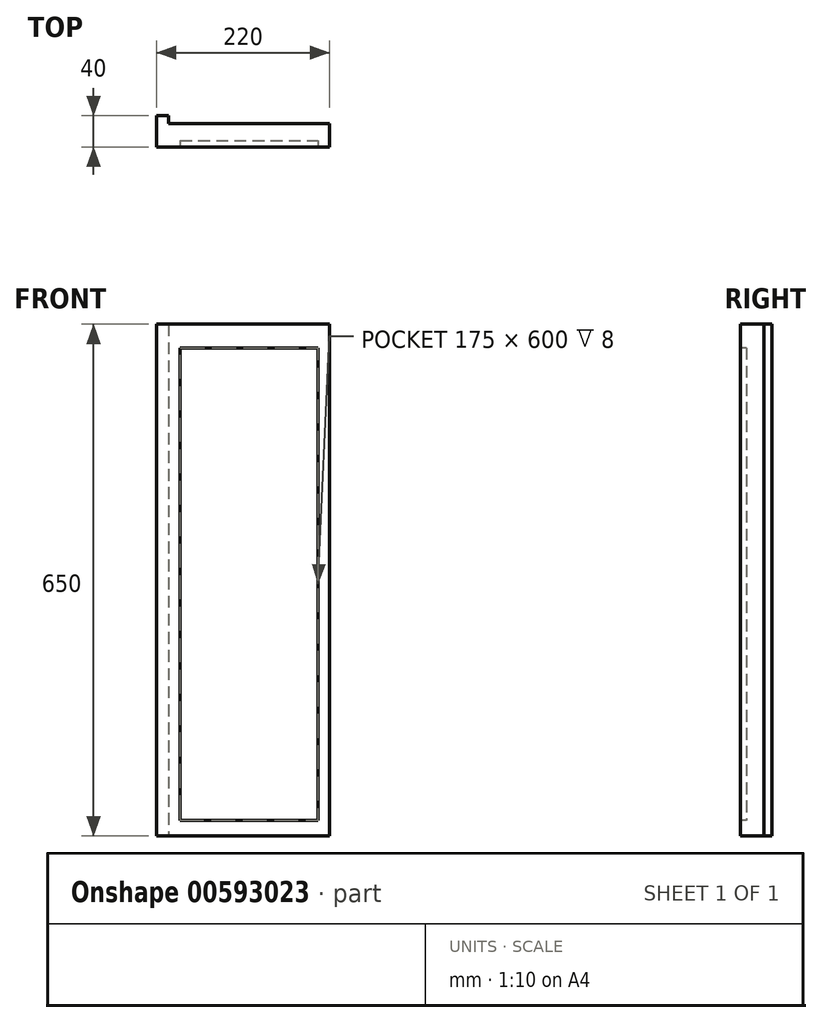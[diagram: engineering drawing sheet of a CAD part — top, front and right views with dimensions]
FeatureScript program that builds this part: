
annotation { "Feature Type Name" : "Feature", "Feature Type Description" : "" }
export const myFeature = defineFeature(function(context is Context, id is Id, definition is map)
    precondition{}
    {
        {
            var Q0;
            Q0=qCreatedBy(makeId("Front.planeOp"),FACE);
            var sketch = newSketch(context, id + "F0", { "sketchPlane" : qUnion([Q0])});
            skLineSegment(sketch, "E0.bottom", {"start": v(0, 0) * mm, "end": v(220, 0) * mm});
            skLineSegment(sketch, "E0.top", {"start": v(0, 650) * mm, "end": v(220, 650) * mm});
            skLineSegment(sketch, "E0.left", {"start": v(0, 0) * mm, "end": v(0, 650) * mm});
            skLineSegment(sketch, "E0.right", {"start": v(220, 0) * mm, "end": v(220, 650) * mm});
            skSolve(sketch);
        }
        {
            var Q0;
            Q0 = qSketchRegion(id + "F0", true);
            extrude(context, id + "F1", {"entities" : qUnion([Q0]), "depth" : 30 * mm, "offsetDistance" : 25 * mm});
        }
        {
            var Q0;
            Q0=makeQuery(id+"F1.opExtrude","CAP_FACE",FACE,{"disambiguationData":[OSD([sQuery(id+"F0.wireOp",EDGE,"E0.bottom"),sQuery(id+"F0.wireOp",EDGE,"E0.top"),sQuery(id+"F0.wireOp",EDGE,"E0.left"),sQuery(id+"F0.wireOp",EDGE,"E0.right")])],"isStart":false});
            var sketch = newSketch(context, id + "F2", { "sketchPlane" : qUnion([Q0])});
            skLineSegment(sketch, "E1.bottom", {"start": v(30, 620) * mm, "end": v(205, 620) * mm});
            skLineSegment(sketch, "E1.top", {"start": v(30, 20) * mm, "end": v(205, 20) * mm});
            skLineSegment(sketch, "E1.left", {"start": v(30, 620) * mm, "end": v(30, 20) * mm});
            skLineSegment(sketch, "E1.right", {"start": v(205, 620) * mm, "end": v(205, 20) * mm});
            skSolve(sketch);
        }
        {
            var Q0;
            Q0=makeQuery(id+"F2.imprint","IMPRINT",FACE,{"disambiguationData":[TD([[makeQuery(id+"F2.imprint","IMPRINT",EDGE,{"derivedFrom":sQuery(id+"F2.wireOp",EDGE,"E1.bottom")}),-1.0]])]});
            extrude(context, id + "F3", {"entities" : qUnion([Q0]), "operationType" : NewBodyOperationType.REMOVE, "oppositeDirection" : true, "depth" : 8 * mm, "offsetDistance" : 25 * mm});
        }
        {
            var Q0;
            Q0=makeQuery(id+"F0.imprint","IMPRINT",FACE,{"disambiguationData":[TD([[makeQuery(id+"F0.imprint","IMPRINT",EDGE,{"derivedFrom":sQuery(id+"F0.wireOp",EDGE,"E0.bottom")}),1.0]])]});
            var sketch = newSketch(context, id + "F4", { "sketchPlane" : qUnion([Q0])});
            skLineSegment(sketch, "E2.bottom", {"start": v(0, 650) * mm, "end": v(15, 650) * mm});
            skLineSegment(sketch, "E2.top", {"start": v(0, 0) * mm, "end": v(15, 0) * mm});
            skLineSegment(sketch, "E2.left", {"start": v(0, 650) * mm, "end": v(0, 0) * mm});
            skLineSegment(sketch, "E2.right", {"start": v(15, 650) * mm, "end": v(15, 0) * mm});
            skSolve(sketch);
        }
        {
            var Q0;
            Q0 = qSketchRegion(id + "F4", true);
            extrude(context, id + "F5", {"entities" : qUnion([Q0]), "operationType" : NewBodyOperationType.ADD, "oppositeDirection" : true, "depth" : 10 * mm, "offsetDistance" : 25 * mm});
        }
    });
